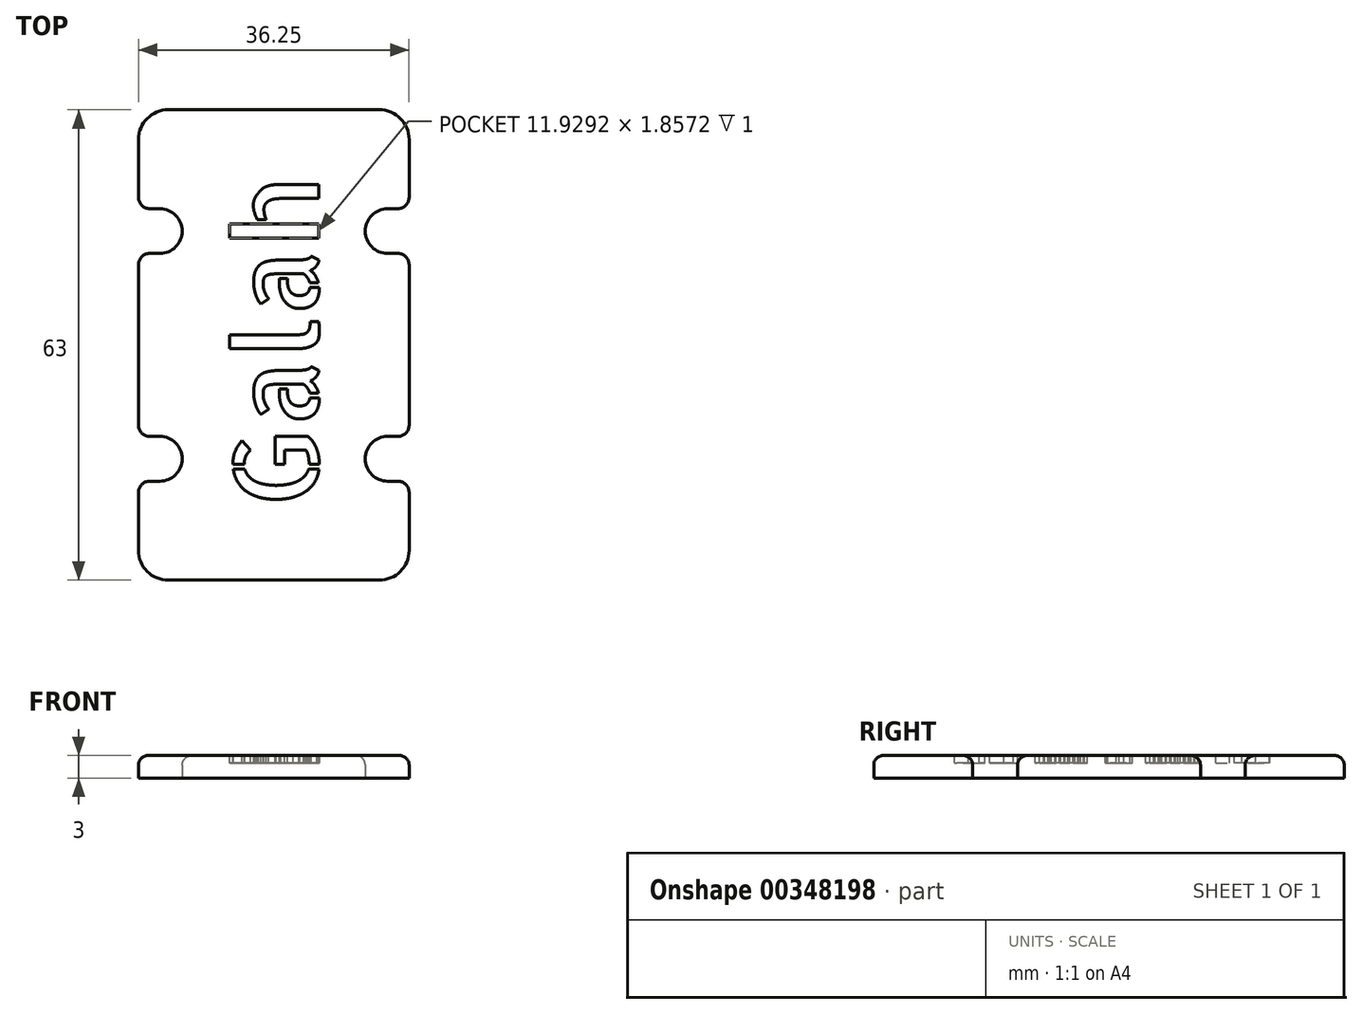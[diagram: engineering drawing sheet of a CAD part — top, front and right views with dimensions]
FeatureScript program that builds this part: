
annotation { "Feature Type Name" : "Feature", "Feature Type Description" : "" }
export const myFeature = defineFeature(function(context is Context, id is Id, definition is map)
    precondition{}
    {
        {
            var Q0;
            Q0=qCreatedBy(makeId("Top.planeOp"),FACE);
            var sketch = newSketch(context, id + "F0", { "sketchPlane" : qUnion([Q0])});
            skLineSegment(sketch, "E0.bottom", {"start": v(18.12, -31.5) * mm, "end": v(-18.12, -31.5) * mm});
            skLineSegment(sketch, "E0.top", {"start": v(18.13, 31.5) * mm, "end": v(-18.12, 31.5) * mm});
            skPoint(sketch, "E0.middle", {"position": v(0, 0) * mm});
            skLineSegment(sketch, "E1", {"start": v(15.25, 18.25) * mm, "end": v(18.13, 18.25) * mm});
            skLineSegment(sketch, "E2", {"start": v(15.25, 12.25) * mm, "end": v(18.13, 12.25) * mm});
            skLineSegment(sketch, "E3", {"start": v(-15.25, 18.25) * mm, "end": v(-18.12, 18.25) * mm});
            skLineSegment(sketch, "E4", {"start": v(-15.25, 12.25) * mm, "end": v(-18.12, 12.25) * mm});
            skLineSegment(sketch, "E5", {"start": v(-15.25, -18.25) * mm, "end": v(-18.12, -18.25) * mm});
            skLineSegment(sketch, "E6", {"start": v(-15.25, -12.25) * mm, "end": v(-18.12, -12.25) * mm});
            skLineSegment(sketch, "E7", {"start": v(15.25, -12.25) * mm, "end": v(18.13, -12.25) * mm});
            skLineSegment(sketch, "E8", {"start": v(15.25, -18.25) * mm, "end": v(18.13, -18.25) * mm});
            skArc(sketch, "E9", {"start": v(15.25, 18.25) * mm, "mid": v(12.25, 15.25) * mm, "end": v(15.25, 12.25) * mm});
            skArc(sketch, "E10", {"start": v(-15.25, 12.25) * mm, "mid": v(-12.25, 15.25) * mm, "end": v(-15.25, 18.25) * mm});
            skArc(sketch, "E11", {"start": v(-15.25, -18.25) * mm, "mid": v(-12.25, -15.25) * mm, "end": v(-15.25, -12.25) * mm});
            skArc(sketch, "E12", {"start": v(15.25, -12.25) * mm, "mid": v(12.25, -15.25) * mm, "end": v(15.25, -18.25) * mm});
            skLineSegment(sketch, "E13", {"start": v(18.13, -18.25) * mm, "end": v(18.13, -31.5) * mm});
            skLineSegment(sketch, "E14", {"start": v(18.13, -12.25) * mm, "end": v(18.13, 12.25) * mm});
            skLineSegment(sketch, "E15", {"start": v(18.13, 18.25) * mm, "end": v(18.13, 31.5) * mm});
            skLineSegment(sketch, "E16", {"start": v(-18.12, 31.5) * mm, "end": v(-18.12, 18.25) * mm});
            skLineSegment(sketch, "E17", {"start": v(-18.12, 12.25) * mm, "end": v(-18.12, -12.25) * mm});
            skLineSegment(sketch, "E18", {"start": v(-18.12, -31.5) * mm, "end": v(-18.12, -18.25) * mm});
            skSolve(sketch);
        }
        {
            var Q0;
            Q0=makeQuery(id+"F0.imprint","IMPRINT",FACE,{"disambiguationData":[TD([[makeQuery(id+"F0.imprint","IMPRINT",EDGE,{"derivedFrom":sQuery(id+"F0.wireOp",EDGE,"E0.bottom")}),-1.0]])]});
            extrude(context, id + "F1", {"entities" : qUnion([Q0]), "depth" : 3 * mm});
        }
        {
            var Q0;
            Q0=makeQuery(id+"F1.opExtrude","SWEPT_EDGE",EDGE,{"disambiguationData":[OSD([sQuery(id+"F0.wireOp",EDGE,"E0.top"),sQuery(id+"F0.wireOp",EDGE,"E15")])]});
            var Q1;
            Q1=makeQuery(id+"F1.opExtrude","SWEPT_EDGE",EDGE,{"disambiguationData":[OSD([sQuery(id+"F0.wireOp",EDGE,"E0.top"),sQuery(id+"F0.wireOp",EDGE,"E16")])]});
            var Q2;
            Q2=makeQuery(id+"F1.opExtrude","SWEPT_EDGE",EDGE,{"disambiguationData":[OSD([sQuery(id+"F0.wireOp",EDGE,"E0.bottom"),sQuery(id+"F0.wireOp",EDGE,"E18")])]});
            var Q3;
            Q3=makeQuery(id+"F1.opExtrude","SWEPT_EDGE",EDGE,{"disambiguationData":[OSD([sQuery(id+"F0.wireOp",EDGE,"E0.bottom"),sQuery(id+"F0.wireOp",EDGE,"E13")])]});
            fillet(context, id + "F2", {"entities" : qUnion([Q0, Q1, Q2, Q3]), "radius" : 4 * mm, "tangentPropagation" : true, "allowEdgeOverflow" : false});
        }
        {
            var Q0;
            Q0=makeQuery(id+"F1.opExtrude","SWEPT_EDGE",EDGE,{"disambiguationData":[OSD([sQuery(id+"F0.wireOp",EDGE,"E1"),sQuery(id+"F0.wireOp",EDGE,"E15")])]});
            var Q1;
            Q1=makeQuery(id+"F1.opExtrude","SWEPT_EDGE",EDGE,{"disambiguationData":[OSD([sQuery(id+"F0.wireOp",EDGE,"E2"),sQuery(id+"F0.wireOp",EDGE,"E14")])]});
            var Q2;
            Q2=makeQuery(id+"F1.opExtrude","SWEPT_EDGE",EDGE,{"disambiguationData":[OSD([sQuery(id+"F0.wireOp",EDGE,"E7"),sQuery(id+"F0.wireOp",EDGE,"E14")])]});
            var Q3;
            Q3=makeQuery(id+"F1.opExtrude","SWEPT_EDGE",EDGE,{"disambiguationData":[OSD([sQuery(id+"F0.wireOp",EDGE,"E8"),sQuery(id+"F0.wireOp",EDGE,"E13")])]});
            var Q4;
            Q4=makeQuery(id+"F1.opExtrude","SWEPT_EDGE",EDGE,{"disambiguationData":[OSD([sQuery(id+"F0.wireOp",EDGE,"E6"),sQuery(id+"F0.wireOp",EDGE,"E17")])]});
            var Q5;
            Q5=makeQuery(id+"F1.opExtrude","SWEPT_EDGE",EDGE,{"disambiguationData":[OSD([sQuery(id+"F0.wireOp",EDGE,"E5"),sQuery(id+"F0.wireOp",EDGE,"E18")])]});
            var Q6;
            Q6=makeQuery(id+"F1.opExtrude","SWEPT_EDGE",EDGE,{"disambiguationData":[OSD([sQuery(id+"F0.wireOp",EDGE,"E3"),sQuery(id+"F0.wireOp",EDGE,"E16")])]});
            var Q7;
            Q7=makeQuery(id+"F1.opExtrude","SWEPT_EDGE",EDGE,{"disambiguationData":[OSD([sQuery(id+"F0.wireOp",EDGE,"E4"),sQuery(id+"F0.wireOp",EDGE,"E17")])]});
            fillet(context, id + "F3", {"entities" : qUnion([Q0, Q1, Q2, Q3, Q4, Q5, Q6, Q7]), "radius" : 1.5 * mm, "tangentPropagation" : true, "allowEdgeOverflow" : false});
        }
        {
            var Q0;
            Q0=makeQuery(id+"F1.opExtrude","CAP_FACE",FACE,{"disambiguationData":[OSD([sQuery(id+"F0.wireOp",EDGE,"E0.bottom"),sQuery(id+"F0.wireOp",EDGE,"E0.top"),sQuery(id+"F0.wireOp",EDGE,"E1"),sQuery(id+"F0.wireOp",EDGE,"E2"),sQuery(id+"F0.wireOp",EDGE,"E3"),sQuery(id+"F0.wireOp",EDGE,"E4"),sQuery(id+"F0.wireOp",EDGE,"E5"),sQuery(id+"F0.wireOp",EDGE,"E6"),sQuery(id+"F0.wireOp",EDGE,"E7"),sQuery(id+"F0.wireOp",EDGE,"E8"),sQuery(id+"F0.wireOp",EDGE,"E9"),sQuery(id+"F0.wireOp",EDGE,"E10"),sQuery(id+"F0.wireOp",EDGE,"E11"),sQuery(id+"F0.wireOp",EDGE,"E12"),sQuery(id+"F0.wireOp",EDGE,"E13"),sQuery(id+"F0.wireOp",EDGE,"E14"),sQuery(id+"F0.wireOp",EDGE,"E15"),sQuery(id+"F0.wireOp",EDGE,"E16"),sQuery(id+"F0.wireOp",EDGE,"E17"),sQuery(id+"F0.wireOp",EDGE,"E18")])],"isStart":false});
            fillet(context, id + "F4", {"entities" : qUnion([Q0]), "radius" : 1.25 * mm, "tangentPropagation" : true, "allowEdgeOverflow" : false});
        }
        {
            var Q0;
            Q0=makeQuery(id+"F1.opExtrude","CAP_FACE",FACE,{"disambiguationData":[OSD([sQuery(id+"F0.wireOp",EDGE,"E0.bottom"),sQuery(id+"F0.wireOp",EDGE,"E0.top"),sQuery(id+"F0.wireOp",EDGE,"E1"),sQuery(id+"F0.wireOp",EDGE,"E2"),sQuery(id+"F0.wireOp",EDGE,"E3"),sQuery(id+"F0.wireOp",EDGE,"E4"),sQuery(id+"F0.wireOp",EDGE,"E5"),sQuery(id+"F0.wireOp",EDGE,"E6"),sQuery(id+"F0.wireOp",EDGE,"E7"),sQuery(id+"F0.wireOp",EDGE,"E8"),sQuery(id+"F0.wireOp",EDGE,"E9"),sQuery(id+"F0.wireOp",EDGE,"E10"),sQuery(id+"F0.wireOp",EDGE,"E11"),sQuery(id+"F0.wireOp",EDGE,"E12"),sQuery(id+"F0.wireOp",EDGE,"E13"),sQuery(id+"F0.wireOp",EDGE,"E14"),sQuery(id+"F0.wireOp",EDGE,"E15"),sQuery(id+"F0.wireOp",EDGE,"E16"),sQuery(id+"F0.wireOp",EDGE,"E17"),sQuery(id+"F0.wireOp",EDGE,"E18")])],"isStart":false});
            var sketch = newSketch(context, id + "F5", { "sketchPlane" : qUnion([Q0])});
            skText(sketch, "E19", { "text": "Galah", "fontName": "AllertaStencil-Regular.ttf"});
            const initialGuessF5  = {"E19": [0.00602, -0.0219, 0, 1, 0.01132]};
            skSetInitialGuess(sketch, initialGuessF5);
            skSolve(sketch);
        }
        {
            var Q0;
            Q0 = qSketchRegion(id + "F5", true);
            extrude(context, id + "F6", {"entities" : qUnion([Q0]), "operationType" : NewBodyOperationType.REMOVE, "oppositeDirection" : true, "depth" : 1 * mm});
        }
    });
